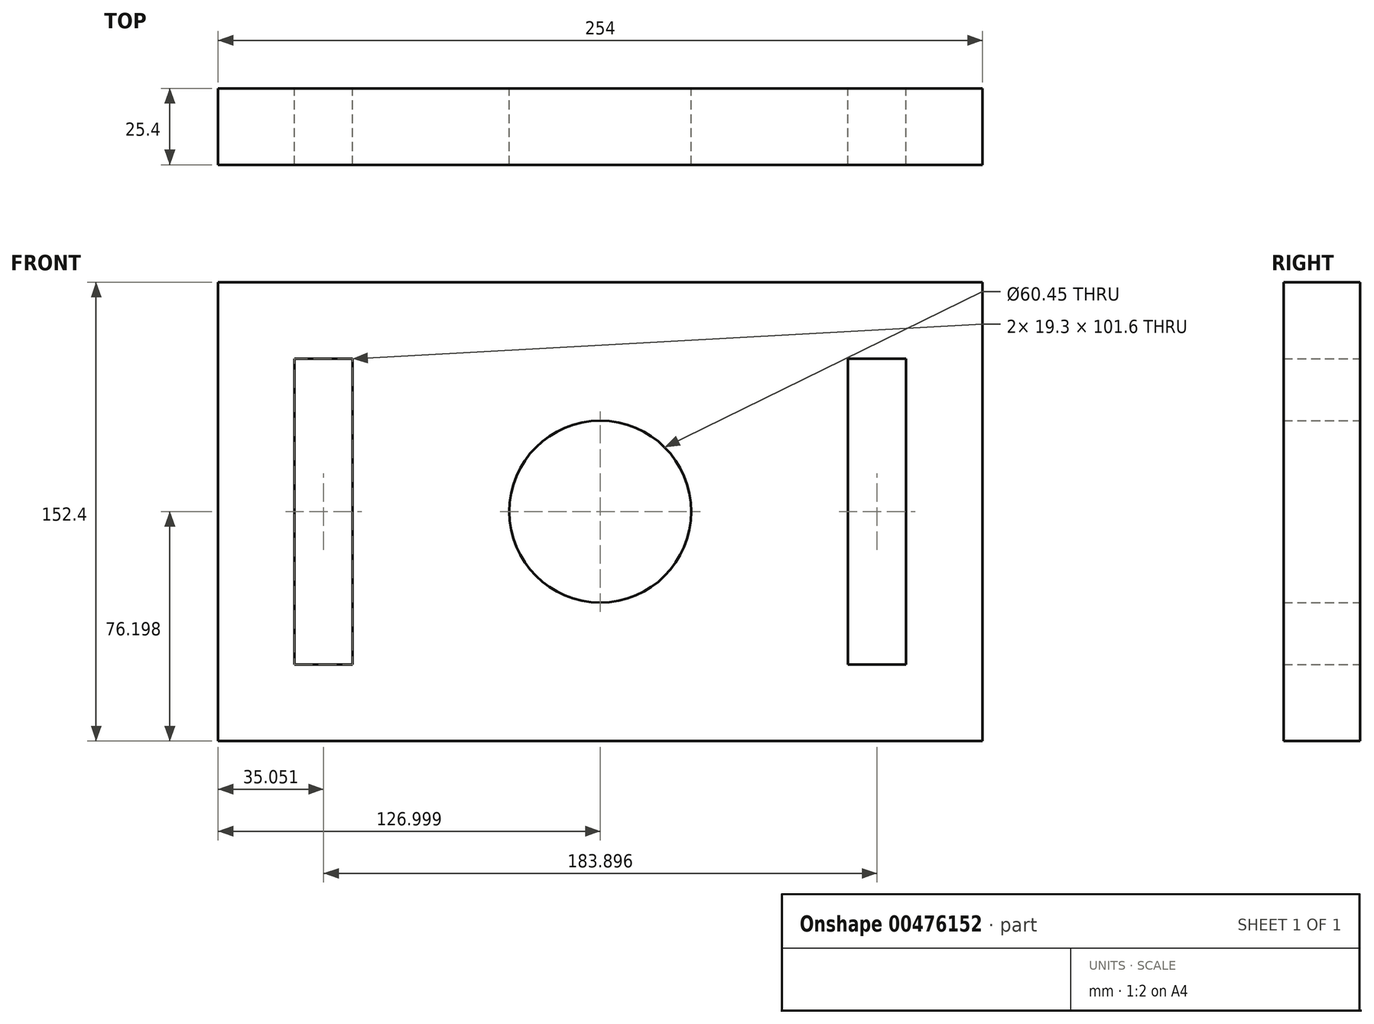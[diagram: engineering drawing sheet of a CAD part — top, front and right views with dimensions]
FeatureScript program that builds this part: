
annotation { "Feature Type Name" : "Feature", "Feature Type Description" : "" }
export const myFeature = defineFeature(function(context is Context, id is Id, definition is map)
    precondition{}
    {
        {
            var Q0;
            Q0=qCreatedBy(makeId("Front.planeOp"),FACE);
            var sketch = newSketch(context, id + "F0", { "sketchPlane" : qUnion([Q0])});
            skLineSegment(sketch, "E0.bottom", {"start": v(-104.64, 83.93) * mm, "end": v(149.36, 83.93) * mm});
            skLineSegment(sketch, "E0.top", {"start": v(-104.64, -68.47) * mm, "end": v(149.36, -68.47) * mm});
            skLineSegment(sketch, "E0.left", {"start": v(-104.64, 83.93) * mm, "end": v(-104.64, -68.47) * mm});
            skLineSegment(sketch, "E0.right", {"start": v(149.36, 83.93) * mm, "end": v(149.36, -68.47) * mm});
            skLineSegment(sketch, "E1.bottom", {"start": v(-79.24, 58.53) * mm, "end": v(-59.94, 58.53) * mm});
            skLineSegment(sketch, "E1.top", {"start": v(-79.24, -43.07) * mm, "end": v(-59.94, -43.07) * mm});
            skLineSegment(sketch, "E1.left", {"start": v(-79.24, 58.53) * mm, "end": v(-79.24, -43.07) * mm});
            skLineSegment(sketch, "E1.right", {"start": v(-59.94, 58.53) * mm, "end": v(-59.94, -43.07) * mm});
            skLineSegment(sketch, "E2", {"start": v(22.36, 83.93) * mm, "end": v(22.36, -68.47) * mm});
            skLineSegment(sketch, "E3.MirrorCS", {"start": v(104.66, 58.53) * mm, "end": v(104.66, -43.07) * mm});
            skLineSegment(sketch, "E4.MirrorCS", {"start": v(123.96, 58.53) * mm, "end": v(123.96, -43.07) * mm});
            skLineSegment(sketch, "E5.MirrorCS", {"start": v(123.96, 58.53) * mm, "end": v(104.66, 58.53) * mm});
            skLineSegment(sketch, "E6.MirrorCS", {"start": v(123.96, -43.07) * mm, "end": v(104.66, -43.07) * mm});
            skCircle(sketch, "E7", {"center": v(22.36, 7.73) * mm, "radius": 30.23 * mm});
            skSolve(sketch);
        }
        {
            var Q0;
            {var subQ4=sQuery(id+"F0.wireOp",EDGE,"E0.left");Q0=makeQuery(id+"F0.imprint","IMPRINT",FACE,{"disambiguationData":[TD([[makeQuery(id+"F0.imprint","IMPRINT",EDGE,{"derivedFrom":subQ4}),1.0]])]});}
            var Q1;
            {var subQ5=sQuery(id+"F0.wireOp",EDGE,"E0.right");Q1=makeQuery(id+"F0.imprint","IMPRINT",FACE,{"disambiguationData":[TD([[makeQuery(id+"F0.imprint","IMPRINT",EDGE,{"derivedFrom":subQ5}),-1.0]])]});}
            extrude(context, id + "F1", {"entities" : qUnion([Q0, Q1]), "depth" : 25.4 * mm});
        }
    });
